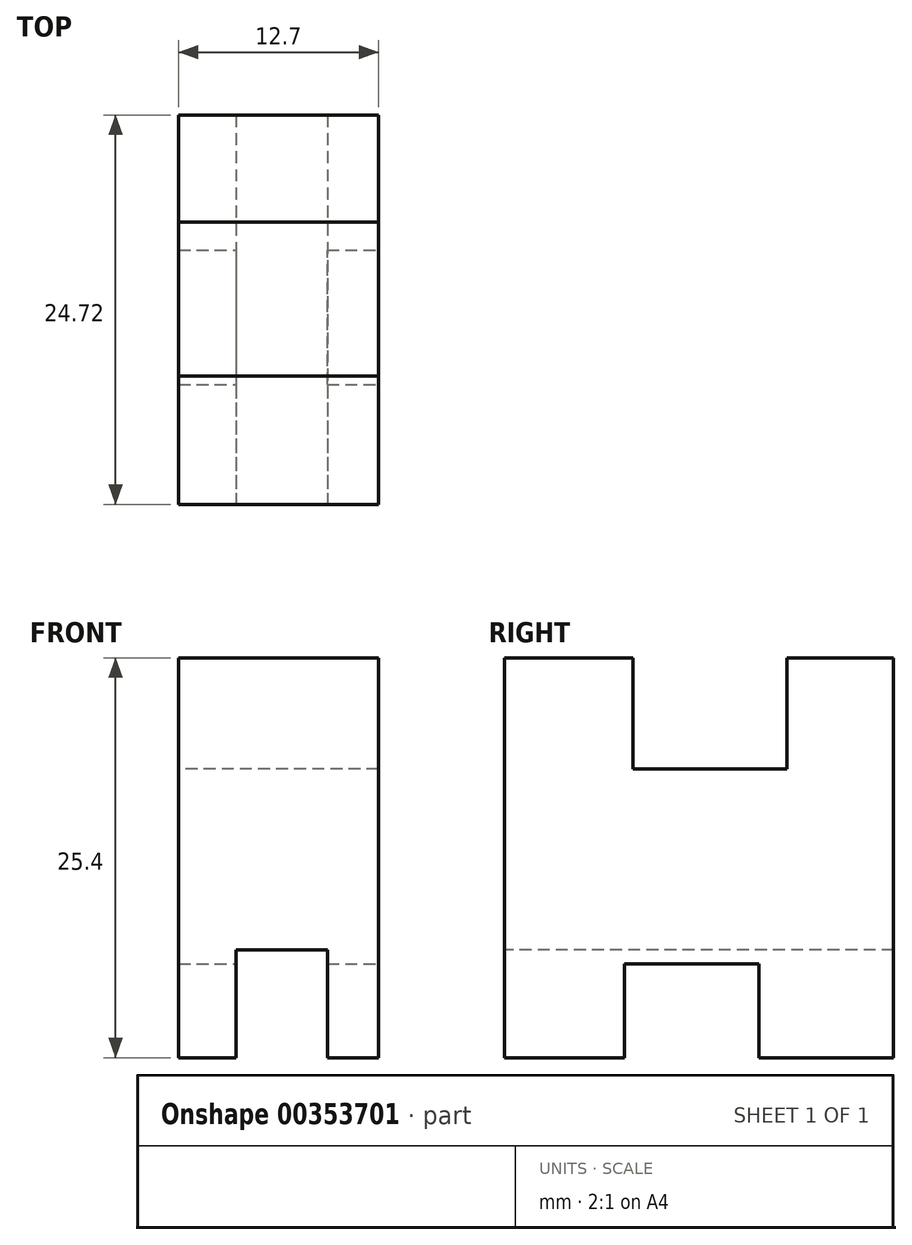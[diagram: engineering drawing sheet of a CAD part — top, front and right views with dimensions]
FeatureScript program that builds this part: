
annotation { "Feature Type Name" : "Feature", "Feature Type Description" : "" }
export const myFeature = defineFeature(function(context is Context, id is Id, definition is map)
    precondition{}
    {
        {
            var Q0;
            Q0=qCreatedBy(makeId("Right.planeOp"),FACE);
            var sketch = newSketch(context, id + "F0", { "sketchPlane" : qUnion([Q0])});
            skLineSegment(sketch, "E0", {"start": v(12.5, 0) * mm, "end": v(12.5, 25.4) * mm});
            skLineSegment(sketch, "E1", {"start": v(12.5, 25.4) * mm, "end": v(20.65, 25.4) * mm});
            skLineSegment(sketch, "E2", {"start": v(20.65, 25.4) * mm, "end": v(20.65, 18.34) * mm});
            skLineSegment(sketch, "E3", {"start": v(20.65, 18.34) * mm, "end": v(30.43, 18.34) * mm});
            skLineSegment(sketch, "E4", {"start": v(30.43, 18.07) * mm, "end": v(30.43, 25.4) * mm});
            skLineSegment(sketch, "E5", {"start": v(30.43, 25.4) * mm, "end": v(37.22, 25.4) * mm});
            skLineSegment(sketch, "E6", {"start": v(37.22, 25.4) * mm, "end": v(37.22, 0) * mm});
            skLineSegment(sketch, "E7", {"start": v(37.22, 0) * mm, "end": v(12.5, 0) * mm});
            skSolve(sketch);
        }
        {
            var Q0;
            Q0=makeQuery(id+"F0.imprint","IMPRINT",FACE,{"disambiguationData":[TD([[makeQuery(id+"F0.imprint","IMPRINT",EDGE,{"derivedFrom":sQuery(id+"F0.wireOp",EDGE,"E0")}),-1.0]])]});
            extrude(context, id + "F1", {"entities" : qUnion([Q0]), "depth" : 12.7 * mm});
        }
        {
            var Q0;
            Q0=makeQuery(id+"F1.opExtrude","CAP_FACE",FACE,{"disambiguationData":[OSD([sQuery(id+"F0.wireOp",EDGE,"E0"),sQuery(id+"F0.wireOp",EDGE,"E1"),sQuery(id+"F0.wireOp",EDGE,"E2"),sQuery(id+"F0.wireOp",EDGE,"E3"),sQuery(id+"F0.wireOp",EDGE,"E4"),sQuery(id+"F0.wireOp",EDGE,"E5"),sQuery(id+"F0.wireOp",EDGE,"E6"),sQuery(id+"F0.wireOp",EDGE,"E7")])],"isStart":false});
            var sketch = newSketch(context, id + "F2", { "sketchPlane" : qUnion([Q0])});
            skLineSegment(sketch, "E8", {"start": v(20.12, 0) * mm, "end": v(20.12, 5.94) * mm});
            skLineSegment(sketch, "E9", {"start": v(20.12, 5.94) * mm, "end": v(28.65, 5.94) * mm});
            skLineSegment(sketch, "E10", {"start": v(28.65, 5.94) * mm, "end": v(28.65, 0) * mm});
            skLineSegment(sketch, "E11", {"start": v(28.65, 0) * mm, "end": v(20.12, 0) * mm});
            skSolve(sketch);
        }
        {
            var Q0;
            Q0=makeQuery(id+"F2.imprint","IMPRINT",FACE,{"disambiguationData":[TD([[makeQuery(id+"F2.imprint","IMPRINT",EDGE,{"derivedFrom":sQuery(id+"F2.wireOp",EDGE,"E8")}),-1.0]])]});
            extrude(context, id + "F3", {"entities" : qUnion([Q0]), "operationType" : NewBodyOperationType.REMOVE, "oppositeDirection" : true, "depth" : 12.7 * mm});
        }
        {
            var Q0;
            Q0=qCreatedBy(makeId("Front.planeOp"),FACE);
            var sketch = newSketch(context, id + "F4", { "sketchPlane" : qUnion([Q0])});
            skLineSegment(sketch, "E12", {"start": v(3.66, 0) * mm, "end": v(3.66, 6.86) * mm});
            skLineSegment(sketch, "E13", {"start": v(3.66, 6.86) * mm, "end": v(9.45, 6.86) * mm});
            skLineSegment(sketch, "E14", {"start": v(9.45, 6.86) * mm, "end": v(9.45, 0) * mm});
            skLineSegment(sketch, "E15", {"start": v(9.45, 0) * mm, "end": v(3.66, 0) * mm});
            skSolve(sketch);
        }
        {
            var Q0;
            Q0=makeQuery(id+"F4.imprint","IMPRINT",FACE,{"disambiguationData":[TD([[makeQuery(id+"F4.imprint","IMPRINT",EDGE,{"derivedFrom":sQuery(id+"F4.wireOp",EDGE,"E12")}),-1.0]])]});
            extrude(context, id + "F5", {"entities" : qUnion([Q0]), "operationType" : NewBodyOperationType.REMOVE, "oppositeDirection" : true, "depth" : 12.7 * mm});
        }
        {
            var Q0;
            Q0=makeQuery(id+"F5.boolean.opBoolean","COPY",FACE,{"derivedFrom":makeQuery(id+"F5.opExtrude","CAP_FACE",FACE,{"disambiguationData":[OSD([sQuery(id+"F4.wireOp",EDGE,"E12"),sQuery(id+"F4.wireOp",EDGE,"E13"),sQuery(id+"F4.wireOp",EDGE,"E14"),sQuery(id+"F4.wireOp",EDGE,"E15")])],"isStart":false})});
            extrude(context, id + "F6", {"entities" : qUnion([Q0]), "operationType" : NewBodyOperationType.REMOVE, "oppositeDirection" : true, "depth" : 25.4 * mm});
        }
    });
